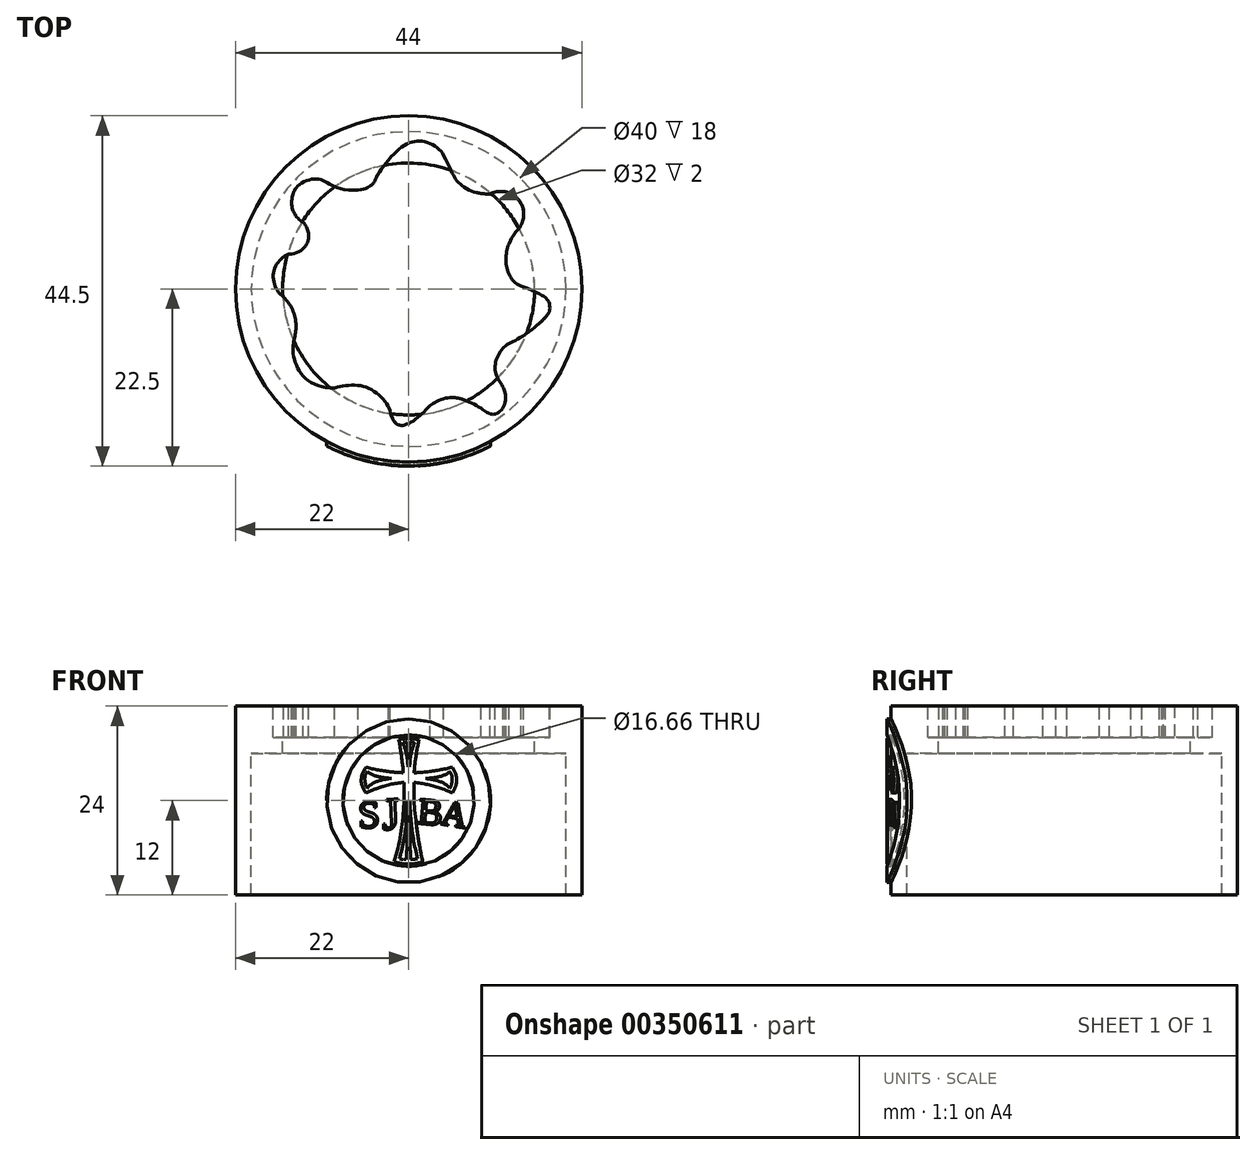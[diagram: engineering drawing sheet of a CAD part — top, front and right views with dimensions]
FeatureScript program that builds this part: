
annotation { "Feature Type Name" : "Feature", "Feature Type Description" : "" }
export const myFeature = defineFeature(function(context is Context, id is Id, definition is map)
    precondition{}
    {
        {
            var Q0;
            Q0=qCreatedBy(makeId("Top.planeOp"),FACE);
            var Q1;
            Q1 = qBodyType(qCreatedBy(id + "F1" ,EDGE), BodyType.WIRE);
            cPlane(context, id + "F0", {"entities" : qUnion([Q0, Q1]), "cplaneType" : CPlaneType.OFFSET, "offset" : 12 * mm, "width" : 150 * mm, "height" : 150 * mm});
        }
        {
            var Q0;
            Q0=qCreatedBy(id+"F0.planeOp",FACE);
            var sketch = newSketch(context, id + "F1", { "sketchPlane" : qUnion([Q0])});
            skCircle(sketch, "E0", {"center": v(0, 0) * mm, "radius": 22 * mm});
            skFitSpline(sketch, "E1", {"points": [v(-14.3, 12.84) * mm, v(-11.44, 13.95) * mm, v(-6.4, 12.53) * mm], "startDerivative": vector(4.46, 5.6) * mm, "endDerivative": vector(16.32, 0.58) * mm});
            skFitSpline(sketch, "E2", {"points": [v(-14.3, 12.84) * mm, v(-14.8, 10.36) * mm, v(-13.38, 8.48) * mm], "startDerivative": vector(-2.91, -3.74) * mm, "endDerivative": vector(4.44, -2.3) * mm});
            skFitSpline(sketch, "E3", {"points": [v(-13.38, 8.48) * mm, v(-12.7, 6.62) * mm, v(-15.26, 4.45) * mm], "startDerivative": vector(2.5, -2.67) * mm, "endDerivative": vector(-9.07, 0.1) * mm});
            skFitSpline(sketch, "E4", {"points": [v(-15.26, 4.45) * mm, v(-17.17, 1.96) * mm, v(-15.87, -1.05) * mm], "startDerivative": vector(-5.88, -2.54) * mm, "endDerivative": vector(5.37, -3.99) * mm});
            skFitSpline(sketch, "E5", {"points": [v(-15.87, -1.05) * mm, v(-14.36, -3.98) * mm, v(-14.54, -6.45) * mm], "startDerivative": vector(4.6, -4.23) * mm, "endDerivative": vector(-1.12, -5.28) * mm});
            skFitSpline(sketch, "E6", {"points": [v(-14.54, -6.45) * mm, v(-14.3, -9.6) * mm, v(-9.38, -12.57) * mm], "startDerivative": vector(-1.49, -4.88) * mm, "endDerivative": vector(14.07, 0.6) * mm});
            skFitSpline(sketch, "E7", {"points": [v(-9.38, -12.57) * mm, v(-5.16, -12.57) * mm, v(-2.36, -15.43) * mm], "startDerivative": vector(7.18, 2.12) * mm, "endDerivative": vector(2.53, -6.19) * mm});
            skFitSpline(sketch, "E8", {"points": [v(-2.36, -15.43) * mm, v(-0.75, -17.32) * mm, v(2.7, -14.82) * mm], "startDerivative": vector(1.67, -9.42) * mm, "endDerivative": vector(5.03, 5.85) * mm});
            skFitSpline(sketch, "E9", {"points": [v(2.7, -14.82) * mm, v(5.45, -13.78) * mm, v(9.22, -15.14) * mm], "startDerivative": vector(4.06, 3.24) * mm, "endDerivative": vector(7.18, -3.93) * mm});
            skFitSpline(sketch, "E10", {"points": [v(9.22, -15.14) * mm, v(11.11, -15.85) * mm, v(12.13, -12.78) * mm], "startDerivative": vector(4.38, -3.77) * mm, "endDerivative": vector(-2.9, 8.35) * mm});
            skFitSpline(sketch, "E11", {"points": [v(12.13, -12.78) * mm, v(11.06, -10.66) * mm, v(11.96, -7.51) * mm], "startDerivative": vector(-1.65, 4.16) * mm, "endDerivative": vector(4.57, 5.25) * mm});
            skFitSpline(sketch, "E12", {"points": [v(11.96, -7.51) * mm, v(14.65, -5.88) * mm, v(17.91, -2.7) * mm], "startDerivative": vector(3.62, 3.57) * mm, "endDerivative": vector(-0.15, 3.1) * mm});
            skFitSpline(sketch, "E13", {"points": [v(17.91, -2.7) * mm, v(16.74, -0.7) * mm, v(14.28, 0.37) * mm], "startDerivative": vector(0.98, 7.59) * mm, "endDerivative": vector(-4.1, 1.2) * mm});
            skFitSpline(sketch, "E14", {"points": [v(14.28, 0.37) * mm, v(12.43, 2.83) * mm, v(12.74, 5.73) * mm], "startDerivative": vector(-6.41, 2.8) * mm, "endDerivative": vector(2.08, 5.38) * mm});
            skFitSpline(sketch, "E15", {"points": [v(12.74, 5.73) * mm, v(14.05, 7.73) * mm, v(14.57, 9.89) * mm], "startDerivative": vector(4.72, 10.1) * mm, "endDerivative": vector(-1.17, 4.74) * mm});
            skFitSpline(sketch, "E16", {"points": [v(14.57, 9.89) * mm, v(13.17, 12.02) * mm, v(10.32, 12.08) * mm], "startDerivative": vector(0.08, 3.85) * mm, "endDerivative": vector(-4.12, -2.28) * mm});
            skFitSpline(sketch, "E17", {"points": [v(10.32, 12.08) * mm, v(6.46, 13.4) * mm, v(4.44, 16.97) * mm], "startDerivative": vector(-9.93, -0.41) * mm, "endDerivative": vector(-5.62, 10.83) * mm});
            skFitSpline(sketch, "E18", {"points": [v(4.44, 16.97) * mm, v(1.52, 18.8) * mm, v(-2.58, 16.4) * mm], "startDerivative": vector(-2.9, 6.35) * mm, "endDerivative": vector(-8.38, -9.56) * mm});
            skFitSpline(sketch, "E19", {"points": [v(-2.58, 16.4) * mm, v(-4.36, 13.61) * mm, v(-6.4, 12.53) * mm], "startDerivative": vector(-9.43, -11.95) * mm, "endDerivative": vector(-8.2, -1.4) * mm});
            skCircle(sketch, "E20", {"center": v(0, 0) * mm, "radius": 20 * mm});
            skSolve(sketch);
        }
        {
            var Q0;
            Q0=qCreatedBy(makeId("Top.planeOp"),FACE);
            cPlane(context, id + "F2", {"entities" : qUnion([Q0]), "cplaneType" : CPlaneType.OFFSET, "offset" : 8 * mm, "width" : 150 * mm, "height" : 150 * mm});
        }
        {
            var Q0;
            Q0=qCreatedBy(id+"F2.planeOp",FACE);
            var sketch = newSketch(context, id + "F3", { "sketchPlane" : qUnion([Q0])});
            skCircle(sketch, "E21", {"center": v(0, 0) * mm, "radius": 20 * mm});
            skCircle(sketch, "E22", {"center": v(0, 0) * mm, "radius": 16 * mm});
            skSolve(sketch);
        }
        {
            var Q0;
            Q0=makeQuery(id+"F1.imprint","IMPRINT",FACE,{"disambiguationData":[TD([[makeQuery(id+"F1.imprint","IMPRINT",EDGE,{"derivedFrom":sQuery(id+"F1.wireOp",EDGE,"E1")}),1.0]])]});
            extrude(context, id + "F4", {"entities" : qUnion([Q0]), "oppositeDirection" : true, "depth" : 4 * mm});
        }
        {
            var Q0;
            Q0=makeQuery(id+"F1.imprint","IMPRINT",FACE,{"disambiguationData":[TD([[makeQuery(id+"F1.imprint","IMPRINT",EDGE,{"derivedFrom":sQuery(id+"F1.wireOp",EDGE,"E0")}),1.0]])]});
            extrude(context, id + "F5", {"entities" : qUnion([Q0]), "operationType" : NewBodyOperationType.ADD, "oppositeDirection" : true, "depth" : 24 * mm});
        }
        {
            var Q0;
            Q0=makeQuery(id+"F3.imprint","IMPRINT",FACE,{"disambiguationData":[TD([[makeQuery(id+"F3.imprint","IMPRINT",EDGE,{"derivedFrom":sQuery(id+"F3.wireOp",EDGE,"E21")}),1.0]])]});
            extrude(context, id + "F6", {"entities" : qUnion([Q0]), "operationType" : NewBodyOperationType.ADD, "oppositeDirection" : true, "depth" : 2 * mm});
        }
        {
            var Q0;
            Q0=qCreatedBy(id+"F0.planeOp",FACE);
            var sketch = newSketch(context, id + "F7", { "sketchPlane" : qUnion([Q0])});
            skCircle(sketch, "E23", {"center": v(0, 0) * mm, "radius": 22.5 * mm});
            skSolve(sketch);
        }
        {
            var Q0;
            Q0 = qSketchRegion(id + "F7", true);
            var Q1;
            Q1 = qConstructionFilter(qBodyType(qCreatedBy(id + "F7" ,EDGE), BodyType.WIRE), ConstructionObject.NO);
            extrude(context, id + "F8", {"entities" : qUnion([Q0]), "bodyType" : ToolBodyType.SURFACE, "operationType" : NewBodyOperationType.ADD, "surfaceEntities" : qUnion([Q1]), "oppositeDirection" : true, "depth" : 24 * mm});
        }
        {
            var Q0;
            Q0=qCreatedBy(makeId("Front.planeOp"),FACE);
            var sketch = newSketch(context, id + "F9", { "sketchPlane" : qUnion([Q0])});
            skCircle(sketch, "E24", {"center": v(0, 0) * mm, "radius": 10.4 * mm});
            skCircle(sketch, "E25", {"center": v(0, 0) * mm, "radius": 8.33 * mm});
            skFitSpline(sketch, "E26", {"points": [v(-1.25, 7.76) * mm, v(0, 7.9) * mm, v(1.33, 7.74) * mm], "startDerivative": vector(2.07, 0.34) * mm, "endDerivative": vector(2.72, -0.55) * mm});
            skFitSpline(sketch, "E27", {"points": [v(-1.25, 7.76) * mm, v(-0.9, 5.48) * mm, v(-0.69, 3.55) * mm], "startDerivative": vector(0.86, -4.43) * mm, "endDerivative": vector(0.2, -4.06) * mm});
            skFitSpline(sketch, "E28", {"points": [v(1.33, 7.74) * mm, v(0.9, 5.49) * mm, v(0.71, 3.55) * mm], "startDerivative": vector(-1.12, -4.38) * mm, "endDerivative": vector(-0.13, -4.03) * mm});
            skFitSpline(sketch, "E29", {"points": [v(-0.69, 3.55) * mm, v(-3.01, 3.77) * mm, v(-5.44, 4.25) * mm], "startDerivative": vector(-4.88, 0.03) * mm, "endDerivative": vector(-4.73, 1.35) * mm});
            skFitSpline(sketch, "E30", {"points": [v(-5.44, 4.25) * mm, v(-6.03, 2.56) * mm, v(-5.44, 0.97) * mm], "startDerivative": vector(-2.17, -3.33) * mm, "endDerivative": vector(2.13, -3.17) * mm});
            skFitSpline(sketch, "E31", {"points": [v(-5.44, 0.97) * mm, v(-2.99, 1.88) * mm, v(-0.62, 2.3) * mm], "startDerivative": vector(4.81, 2.31) * mm, "endDerivative": vector(6.89, 0.6) * mm});
            skFitSpline(sketch, "E32", {"points": [v(0.71, 3.55) * mm, v(3.05, 3.76) * mm, v(5.55, 4.25) * mm], "startDerivative": vector(4.87, -0.02) * mm, "endDerivative": vector(6.6, 1.66) * mm});
            skFitSpline(sketch, "E33", {"points": [v(5.55, 4.25) * mm, v(6.1, 2.78) * mm, v(5.55, 0.98) * mm], "startDerivative": vector(1.49, -2.64) * mm, "endDerivative": vector(-2.02, -3.2) * mm});
            skFitSpline(sketch, "E34", {"points": [v(5.55, 0.98) * mm, v(2.93, 1.92) * mm, v(0.66, 2.32) * mm], "startDerivative": vector(-7.26, 3.26) * mm, "endDerivative": vector(-6.47, 0.62) * mm});
            skFitSpline(sketch, "E35", {"points": [v(-0.62, 2.3) * mm, v(-0.77, -2.6) * mm, v(-1.83, -7.74) * mm], "startDerivative": vector(0.5, -10.06) * mm, "endDerivative": vector(-3.3, -11.1) * mm});
            skFitSpline(sketch, "E36", {"points": [v(0.66, 2.32) * mm, v(0.92, -2.57) * mm, v(1.79, -7.75) * mm], "startDerivative": vector(-0.06, -13.21) * mm, "endDerivative": vector(2.26, -9.86) * mm});
            skFitSpline(sketch, "E37", {"points": [v(-1.83, -7.74) * mm, v(0, -8.05) * mm, v(1.79, -7.75) * mm], "startDerivative": vector(0.07, -0.52) * mm, "endDerivative": vector(0.48, 0.38) * mm});
            skFitSpline(sketch, "E38", {"points": [v(-5.23, 3.72) * mm, v(-5.56, 2.66) * mm, v(-5.26, 1.56) * mm], "startDerivative": vector(-1.55, -1.52) * mm, "endDerivative": vector(1.07, -2.05) * mm});
            skFitSpline(sketch, "E39", {"points": [v(-5.23, 3.72) * mm, v(-3.97, 3.08) * mm, v(-2.2, 2.83) * mm], "startDerivative": vector(1.39, -1.7) * mm, "endDerivative": vector(2.85, -0.16) * mm});
            skFitSpline(sketch, "E40", {"points": [v(-5.26, 1.56) * mm, v(-4.14, 2.39) * mm, v(-2.2, 2.83) * mm], "startDerivative": vector(0.88, 2.02) * mm, "endDerivative": vector(3.64, 0.38) * mm});
            skFitSpline(sketch, "E41", {"points": [v(2.13, 2.82) * mm, v(3.94, 3.06) * mm, v(5.2, 3.7) * mm], "startDerivative": vector(3.4, 0.17) * mm, "endDerivative": vector(1.3, 1.58) * mm});
            skFitSpline(sketch, "E42", {"points": [v(2.13, 2.82) * mm, v(3.95, 2.43) * mm, v(5.22, 1.56) * mm], "startDerivative": vector(3.58, -0.47) * mm, "endDerivative": vector(1.5, -2.48) * mm});
            skFitSpline(sketch, "E43", {"points": [v(5.2, 3.7) * mm, v(5.54, 2.65) * mm, v(5.22, 1.56) * mm], "startDerivative": vector(1.76, -2.03) * mm, "endDerivative": vector(-1.28, -2.04) * mm});
            skFitSpline(sketch, "E44", {"points": [v(-0.73, 7.35) * mm, v(-0.28, 5.92) * mm, v(-0.09, 4.26) * mm], "startDerivative": vector(1.15, -2.81) * mm, "endDerivative": vector(0.17, -3.77) * mm});
            skFitSpline(sketch, "E45", {"points": [v(-0.09, 4.26) * mm, v(-0.09, 5.98) * mm, v(-0.18, 7.44) * mm], "startDerivative": vector(0.3, 4.02) * mm, "endDerivative": vector(-0.5, 2.52) * mm});
            skFitSpline(sketch, "E46", {"points": [v(-0.73, 7.35) * mm, v(-0.49, 7.42) * mm, v(-0.18, 7.44) * mm], "startDerivative": vector(0.9, 0.39) * mm, "endDerivative": vector(0.81, -0.07) * mm});
            skFitSpline(sketch, "E47", {"points": [v(0.18, 7.44) * mm, v(0.1, 5.84) * mm, v(0.13, 4.26) * mm], "startDerivative": vector(-0.32, -2.95) * mm, "endDerivative": vector(0.12, -0.5) * mm});
            skFitSpline(sketch, "E48", {"points": [v(0.13, 4.26) * mm, v(0.32, 6.03) * mm, v(0.74, 7.33) * mm], "startDerivative": vector(0.3, 3.95) * mm, "endDerivative": vector(0.97, 2.66) * mm});
            skFitSpline(sketch, "E49", {"points": [v(0.18, 7.44) * mm, v(0.47, 7.44) * mm, v(0.74, 7.33) * mm], "startDerivative": vector(-0.1, 0.22) * mm, "endDerivative": vector(0.51, -0.29) * mm});
            skFitSpline(sketch, "E50", {"points": [v(-0.17, 0) * mm, v(-0.52, -4.41) * mm, v(-1.16, -7.37) * mm], "startDerivative": vector(-0.32, -10.88) * mm, "endDerivative": vector(-1.6, -6.24) * mm});
            skFitSpline(sketch, "E51", {"points": [v(-0.17, 0) * mm, v(-0.17, -4.56) * mm, v(-0.3, -7.46) * mm], "startDerivative": vector(0.31, -7.4) * mm, "endDerivative": vector(-0.35, -6.22) * mm});
            skFitSpline(sketch, "E52", {"points": [v(-1.16, -7.37) * mm, v(-0.77, -7.49) * mm, v(-0.3, -7.46) * mm], "startDerivative": vector(0.8, -0.24) * mm, "endDerivative": vector(0.93, 0.05) * mm});
            skFitSpline(sketch, "E53", {"points": [v(0.18, -0.09) * mm, v(0.16, -4.24) * mm, v(0.25, -7.46) * mm], "startDerivative": vector(-0.08, -8.06) * mm, "endDerivative": vector(0.25, -6.71) * mm});
            skFitSpline(sketch, "E54", {"points": [v(1.16, -7.37) * mm, v(0.53, -4.5) * mm, v(0.18, -0.09) * mm], "startDerivative": vector(-1.49, 6.08) * mm, "endDerivative": vector(-0.25, 8.2) * mm});
            skFitSpline(sketch, "E55", {"points": [v(0.25, -7.46) * mm, v(0.66, -7.46) * mm, v(1.16, -7.37) * mm], "startDerivative": vector(0.84, -0.04) * mm, "endDerivative": vector(0.96, 0.22) * mm});
            skSolve(sketch);
        }
        {
            var Q0;
            Q0=qCreatedBy(makeId("Front.planeOp"),FACE);
            var sketch = newSketch(context, id + "F10", { "sketchPlane" : qUnion([Q0])});
            skText(sketch, "E56", { "text": "S", "fontName": "Tinos-Regular.ttf"});
            skText(sketch, "E57", { "text": "J", "fontName": "Tinos-Regular.ttf"});
            skText(sketch, "E58", { "text": "B", "fontName": "Tinos-Regular.ttf"});
            skText(sketch, "E59", { "text": "A", "fontName": "Tinos-Regular.ttf"});
            const initialGuessF10  = {"E56": [-0.00637, -0.00345, 0.99966, 0.02625, 0.00357], "E57": [-0.0033, -0.00366, 0.99908, 0.04292, 0.00416], "E58": [0.00105, -0.00288, 0.9961, -0.0882, 0.0034], "E59": [0.00398, -0.00296, 0.98638, -0.1645, 0.00326]};
            skSetInitialGuess(sketch, initialGuessF10);
            skSolve(sketch);
        }
        {
            var Q0;
            Q0=makeQuery(id+"F9.imprint","IMPRINT",FACE,{"disambiguationData":[TD([[makeQuery(id+"F9.imprint","IMPRINT",EDGE,{"derivedFrom":sQuery(id+"F9.wireOp",EDGE,"E24")}),1.0]])]});
            var Q1;
            Q1=makeQuery(id+"F9.imprint","IMPRINT",FACE,{"disambiguationData":[TD([[makeQuery(id+"F9.imprint","IMPRINT",EDGE,{"derivedFrom":sQuery(id+"F9.wireOp",EDGE,"E26")}),-1.0]])]});
            var Q2;
            Q2 = qSketchRegion(id + "F10", true);
            var Q3;
            Q3=makeQuery(id+"F8.opExtrude","SWEPT_FACE",FACE,{"disambiguationData":[OSD([sQuery(id+"F7.wireOp",EDGE,"E23")])]});
            var Q4;
            Q4=makeQuery(id+"F5.opExtrude","SWEPT_FACE",FACE,{"disambiguationData":[OSD([sQuery(id+"F1.wireOp",EDGE,"E0")])]});
            extrude(context, id + "F11", {"entities" : qUnion([Q0, Q1, Q2]), "operationType" : NewBodyOperationType.ADD, "endBound" : BoundingType.UP_TO_SURFACE, "endBoundEntityFace" : qUnion([Q3]), "depth" : 25 * mm, "hasSecondDirection" : true, "secondDirectionBound" : SecondDirectionBoundingType.UP_TO_SURFACE, "secondDirectionOppositeDirection" : false, "secondDirectionBoundEntityFace" : qUnion([Q4]), "secondDirectionDepth" : 25 * mm});
        }
    });
